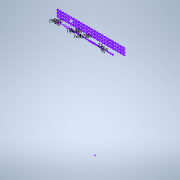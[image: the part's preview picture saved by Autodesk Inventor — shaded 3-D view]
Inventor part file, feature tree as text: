
AUTODESK INVENTOR PART (.ipt)
format: ipt  version: 2021 (Build 250183000, 183)  size: 309,760 bytes
history: native  units: mm
features: sketch x1
ambient origin geometry x8: Origin, YZ Plane, XZ Plane, XY Plane, X Axis, Y Axis, Z Axis, Center Point
feature tree (1):
  sketch  "Esboço1"  dims[d0=10.0mm d1=20.0mm d2=10.0mm d3=90.0deg d4=3.368097mm d5=3.368097mm d6=14.415669mm d7=16.794509mm d8=12.397254mm d9=6.0mm d10=5.0mm d11=5.0mm d12=2.0mm d13=2.0mm]
